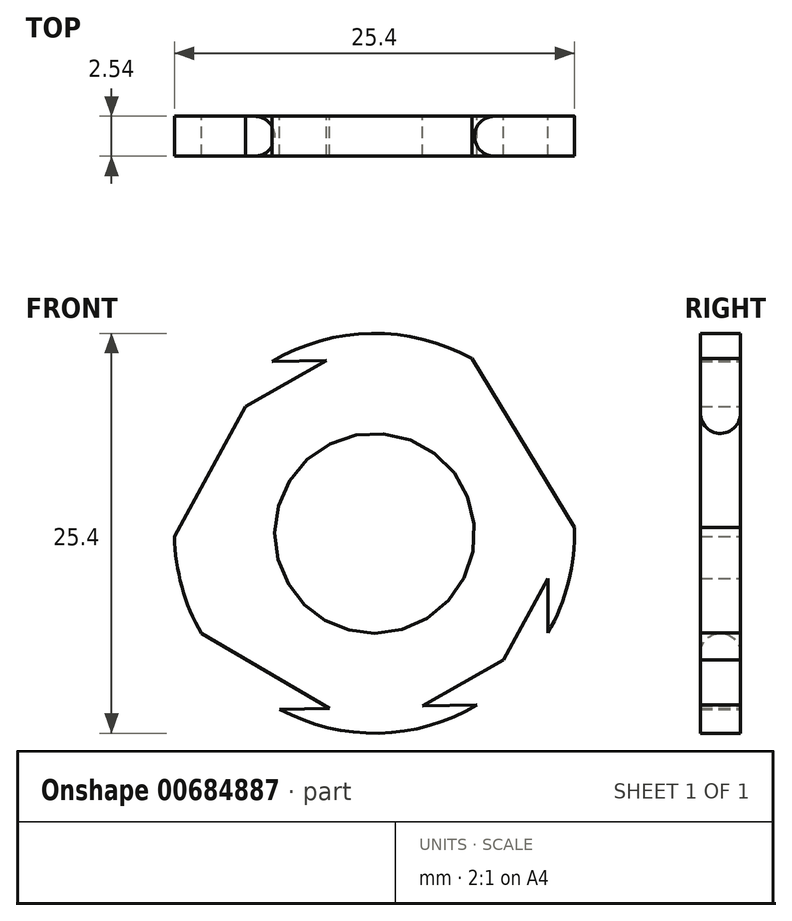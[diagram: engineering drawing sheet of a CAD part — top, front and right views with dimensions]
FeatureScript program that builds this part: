
annotation { "Feature Type Name" : "Feature", "Feature Type Description" : "" }
export const myFeature = defineFeature(function(context is Context, id is Id, definition is map)
    precondition{}
    {
        {
            var Q0;
            Q0=qCreatedBy(makeId("Front.planeOp"),FACE);
            var sketch = newSketch(context, id + "F0", { "sketchPlane" : qUnion([Q0])});
            skCircle(sketch, "E0", {"center": v(0, 0) * mm, "radius": 12.7 * mm});
            skCircle(sketch, "E1", {"center": v(0, 0) * mm, "radius": 6.35 * mm});
            skCircle(sketch, "E2.cCircle", {"center": v(0, 0) * mm, "radius": 11.04 * mm, "construction": true});
            skLineSegment(sketch, "E2.0", {"start": v(-11, 6.43) * mm, "end": v(0.06, 12.75) * mm});
            skLineSegment(sketch, "E2.1", {"start": v(0.06, 12.75) * mm, "end": v(11.07, 6.32) * mm});
            skLineSegment(sketch, "E2.2", {"start": v(11.07, 6.32) * mm, "end": v(11, -6.43) * mm});
            skLineSegment(sketch, "E2.3", {"start": v(11, -6.43) * mm, "end": v(-0.06, -12.75) * mm});
            skLineSegment(sketch, "E2.4", {"start": v(-0.06, -12.75) * mm, "end": v(-11.07, -6.32) * mm});
            skLineSegment(sketch, "E2.5", {"start": v(-11.07, -6.32) * mm, "end": v(-11, 6.43) * mm});
            skPoint(sketch, "E2.0.midPoint", {"position": v(-5.47, 9.59) * mm});
            skLineSegment(sketch, "E3.0", {"start": v(6.13, 11.18) * mm, "end": v(12.75, 0.28) * mm});
            skLineSegment(sketch, "E3.1", {"start": v(12.75, 0.28) * mm, "end": v(6.62, -10.9) * mm});
            skLineSegment(sketch, "E3.2", {"start": v(6.62, -10.9) * mm, "end": v(-6.13, -11.18) * mm});
            skLineSegment(sketch, "E3.3", {"start": v(-6.13, -11.18) * mm, "end": v(-12.75, -0.28) * mm});
            skLineSegment(sketch, "E3.4", {"start": v(-12.75, -0.28) * mm, "end": v(-6.62, 10.9) * mm});
            skLineSegment(sketch, "E3.5", {"start": v(-6.62, 10.9) * mm, "end": v(6.13, 11.18) * mm});
            skPoint(sketch, "E3.0.midPoint", {"position": v(9.44, 5.73) * mm});
            skSolve(sketch);
        }
        {
            var Q0;
            Q0=makeQuery(id+"F0.imprint","IMPRINT",FACE,{"disambiguationData":[TD([[makeQuery(id+"F0.imprint","IMPRINT",EDGE,{"derivedFrom":sQuery(id+"F0.wireOp",EDGE,"E1")}),-1.0]])]});
            var Q1;
            {var subQ0=sQuery(id+"F0.wireOp",EDGE,"E2.1");var subQ1=sQuery(id+"F0.wireOp",EDGE,"E0");var subQ2=makeQuery(id+"F0.imprint","INTERSECT",VERTEX,{"disambiguationData":[OD(1.0)],"derivedFrom":[subQ1,subQ0]});Q1=makeQuery(id+"F0.imprint","IMPRINT",FACE,{"disambiguationData":[TD([[makeQuery(id+"F0.imprint","IMPRINT",EDGE,{"disambiguationData":[TD([[subQ2,-1.0]])],"derivedFrom":subQ1}),1.0]])]});}
            var Q2;
            {var subQ0=sQuery(id+"F0.wireOp",EDGE,"E3.5");var subQ1=sQuery(id+"F0.wireOp",EDGE,"E0");var subQ2=makeQuery(id+"F0.imprint","INTERSECT",VERTEX,{"disambiguationData":[OD(1.0)],"derivedFrom":[subQ1,subQ0]});Q2=makeQuery(id+"F0.imprint","IMPRINT",FACE,{"disambiguationData":[TD([[makeQuery(id+"F0.imprint","IMPRINT",EDGE,{"disambiguationData":[TD([[subQ2,-1.0]])],"derivedFrom":subQ1}),1.0]])]});}
            var Q3;
            {var subQ0=sQuery(id+"F0.wireOp",EDGE,"E2.0");var subQ1=sQuery(id+"F0.wireOp",EDGE,"E0");var subQ2=makeQuery(id+"F0.imprint","INTERSECT",VERTEX,{"disambiguationData":[OD(1.0)],"derivedFrom":[subQ1,subQ0]});Q3=makeQuery(id+"F0.imprint","IMPRINT",FACE,{"disambiguationData":[TD([[makeQuery(id+"F0.imprint","IMPRINT",EDGE,{"disambiguationData":[TD([[subQ2,-1.0]])],"derivedFrom":subQ1}),1.0]])]});}
            var Q4;
            {var subQ0=sQuery(id+"F0.wireOp",EDGE,"E3.4");var subQ1=sQuery(id+"F0.wireOp",EDGE,"E0");var subQ2=makeQuery(id+"F0.imprint","INTERSECT",VERTEX,{"disambiguationData":[OD(1.0)],"derivedFrom":[subQ1,subQ0]});Q4=makeQuery(id+"F0.imprint","IMPRINT",FACE,{"disambiguationData":[TD([[makeQuery(id+"F0.imprint","IMPRINT",EDGE,{"disambiguationData":[TD([[subQ2,-1.0]])],"derivedFrom":subQ1}),1.0]])]});}
            var Q5;
            {var subQ0=sQuery(id+"F0.wireOp",EDGE,"E2.5");var subQ1=sQuery(id+"F0.wireOp",EDGE,"E0");var subQ2=makeQuery(id+"F0.imprint","INTERSECT",VERTEX,{"disambiguationData":[OD(1.0)],"derivedFrom":[subQ1,subQ0]});Q5=makeQuery(id+"F0.imprint","IMPRINT",FACE,{"disambiguationData":[TD([[makeQuery(id+"F0.imprint","IMPRINT",EDGE,{"disambiguationData":[TD([[subQ2,-1.0]])],"derivedFrom":subQ1}),1.0]])]});}
            var Q6;
            {var subQ0=sQuery(id+"F0.wireOp",EDGE,"E3.3");var subQ1=sQuery(id+"F0.wireOp",EDGE,"E0");var subQ2=makeQuery(id+"F0.imprint","INTERSECT",VERTEX,{"disambiguationData":[OD(1.0)],"derivedFrom":[subQ1,subQ0]});Q6=makeQuery(id+"F0.imprint","IMPRINT",FACE,{"disambiguationData":[TD([[makeQuery(id+"F0.imprint","IMPRINT",EDGE,{"disambiguationData":[TD([[subQ2,-1.0]])],"derivedFrom":subQ1}),1.0]])]});}
            var Q7;
            {var subQ0=sQuery(id+"F0.wireOp",EDGE,"E2.4");var subQ1=sQuery(id+"F0.wireOp",EDGE,"E0");var subQ2=makeQuery(id+"F0.imprint","INTERSECT",VERTEX,{"disambiguationData":[OD(1.0)],"derivedFrom":[subQ1,subQ0]});Q7=makeQuery(id+"F0.imprint","IMPRINT",FACE,{"disambiguationData":[TD([[makeQuery(id+"F0.imprint","IMPRINT",EDGE,{"disambiguationData":[TD([[subQ2,-1.0]])],"derivedFrom":subQ1}),1.0]])]});}
            var Q8;
            {var subQ0=sQuery(id+"F0.wireOp",EDGE,"E3.2");var subQ1=sQuery(id+"F0.wireOp",EDGE,"E0");var subQ2=makeQuery(id+"F0.imprint","INTERSECT",VERTEX,{"disambiguationData":[OD(1.0)],"derivedFrom":[subQ1,subQ0]});Q8=makeQuery(id+"F0.imprint","IMPRINT",FACE,{"disambiguationData":[TD([[makeQuery(id+"F0.imprint","IMPRINT",EDGE,{"disambiguationData":[TD([[subQ2,-1.0]])],"derivedFrom":subQ1}),1.0]])]});}
            var Q9;
            {var subQ0=sQuery(id+"F0.wireOp",EDGE,"E2.3");var subQ1=sQuery(id+"F0.wireOp",EDGE,"E0");var subQ2=makeQuery(id+"F0.imprint","INTERSECT",VERTEX,{"disambiguationData":[OD(1.0)],"derivedFrom":[subQ1,subQ0]});Q9=makeQuery(id+"F0.imprint","IMPRINT",FACE,{"disambiguationData":[TD([[makeQuery(id+"F0.imprint","IMPRINT",EDGE,{"disambiguationData":[TD([[subQ2,-1.0]])],"derivedFrom":subQ1}),1.0]])]});}
            var Q10;
            {var subQ0=sQuery(id+"F0.wireOp",EDGE,"E3.0");var subQ1=sQuery(id+"F0.wireOp",EDGE,"E0");var subQ2=makeQuery(id+"F0.imprint","INTERSECT",VERTEX,{"disambiguationData":[OD(0.0)],"derivedFrom":[subQ1,subQ0]});Q10=makeQuery(id+"F0.imprint","IMPRINT",FACE,{"disambiguationData":[TD([[makeQuery(id+"F0.imprint","IMPRINT",EDGE,{"disambiguationData":[TD([[subQ2,1.0]])],"derivedFrom":subQ1}),1.0]])]});}
            var Q11;
            {var subQ0=sQuery(id+"F0.wireOp",EDGE,"E2.2");var subQ1=sQuery(id+"F0.wireOp",EDGE,"E0");var subQ2=makeQuery(id+"F0.imprint","INTERSECT",VERTEX,{"disambiguationData":[OD(0.0)],"derivedFrom":[subQ1,subQ0]});Q11=makeQuery(id+"F0.imprint","IMPRINT",FACE,{"disambiguationData":[TD([[makeQuery(id+"F0.imprint","IMPRINT",EDGE,{"disambiguationData":[TD([[subQ2,-1.0]])],"derivedFrom":subQ1}),1.0]])]});}
            var Q12;
            {var subQ0=sQuery(id+"F0.wireOp",EDGE,"E3.0");var subQ1=sQuery(id+"F0.wireOp",EDGE,"E0");var subQ2=makeQuery(id+"F0.imprint","INTERSECT",VERTEX,{"disambiguationData":[OD(1.0)],"derivedFrom":[subQ1,subQ0]});Q12=makeQuery(id+"F0.imprint","IMPRINT",FACE,{"disambiguationData":[TD([[makeQuery(id+"F0.imprint","IMPRINT",EDGE,{"disambiguationData":[TD([[subQ2,-1.0]])],"derivedFrom":subQ1}),1.0]])]});}
            extrude(context, id + "F1", {"entities" : qUnion([Q0, Q1, Q2, Q3, Q4, Q5, Q6, Q7, Q8, Q9, Q10, Q11, Q12]), "depth" : 2.54 * mm, "offsetDistance" : 25.4 * mm});
        }
        {
            var Q0;
            Q0=makeQuery(id+"F1.opExtrude","CAP_EDGE",EDGE,{"disambiguationData":[OSD([sQuery(id+"F0.wireOp",EDGE,"E1")])],"isStart":false});
            var Q1;
            Q1=makeQuery(id+"F1.opExtrude","CAP_EDGE",EDGE,{"disambiguationData":[OSD([sQuery(id+"F0.wireOp",EDGE,"E1")])],"isStart":true});
            fillet(context, id + "F2", {"entities" : qUnion([Q0, Q1]), "radius" : 1.27 * mm, "tangentPropagation" : true, "allowEdgeOverflow" : false});
        }
    });
